# Revit family: Banco Toledo
name_source: partatom
category: Furniture
units: mm (PartAtom-declared; Revit-internal decimal feet)

## family parameters
Always vertical = Yes
Cut with Voids When Loaded = No
OmniClass Number = 23.40.20.00
OmniClass Title = General Furniture and Specialties
Room Calculation Point = No
Shared = No
Work Plane-Based = No

## types (2) — shared parameters
A = 2 m
Description = Banco fabricado en hormigón prefabricado armado color blanco granítico
Fabricante = BENITO URBAN SL
Ficha_Tecnica = https://www.benito.com
Type Comments = Anclaje recomendado: Apoyado en el suelo en sus extremos robustos
con el objetivo de facilitar la limpieza y el mantenimiento.
URL_Producto = https://www.benito.com
zero-valued in all types: Default Elevation

## per-type parameters (varying)
| type | B | H | H1 | Material | Referencia | UM370-2000mm | UM370RC-2000 |
| Banco Toledo-UM370-2000mm | 0.45 m | 0.425 m | 0 m | <By Category> | UM370 | Yes | No |
| Banco Toledo-UM370RC-2000mm | 0.56 m | 0.845 m | 0.45 m | Hormigón prefabricado | UM370RC | No | Yes |

## geometry (parser evidence)
native form markers: Blend x4, Sweep x6
no freeform markers — native parametric forms only
